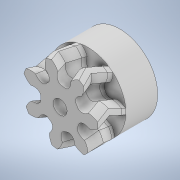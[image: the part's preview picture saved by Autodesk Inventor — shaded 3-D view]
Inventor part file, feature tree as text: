
AUTODESK INVENTOR PART (.ipt)
format: ipt  version: 2022 (Build 260153070, 153G)  size: 865,792 bytes
history: native  units: mm
features: sketch x5, extrude x3, helix x2, pattern_circular x1, mirror x1, revolve x1, projected_geometry x1
ambient origin geometry x8: Origin, YZ Plane, XZ Plane, XY Plane, X Axis, Y Axis, Z Axis, Center Point
bodies: Solid1 (feature_tree)
feature tree (14):
  sketch  "Sketch1"  dims[d0=1.5mm d1=0.0mm]
  extrude  "Extrusion1"  TaperAngle=0.0deg  [1 undecoded]
  helix  "Coil1"  [1 undecoded]
  pattern_circular  "Circular Pattern1"  [2 undecoded]
  mirror  "Mirror1"
  helix  "Coil2"  [1 undecoded]
  extrude  "Extrusion2"  Depth=2.15mm
  extrude  "Extrusion3"  Depth=2.15mm
  revolve  "Revolution1"  Angle=90.0deg
  sketch  "Sketch2"  dims[d2=64.295707mm d3=1.5mm d4=10.0mm d5=0.0mm d6=90.0deg d7=90.0deg d8=0.0mm d9=0.0mm d10=70.0mm d11=360.0deg]
  projected_geometry  "Projected Loop1"
  sketch  "Sketch3"  dims[d13=64.295707mm d14=0.5mm d15=10.0mm d16=0.0mm d17=90.0deg d18=90.0deg d19=0.0mm d20=0.0mm]
  sketch  "Sketch4"  dims[d21=4.0mm d22=0.0mm]
  sketch  "Sketch5"  dims[d23=6.2mm d24=2.0mm d25=0.0mm d26=0.875mm d27=1.5mm d28=2.15mm d29=90.0deg]
note: 5 required parameter values undecoded (feature->parameter linkage not recoverable at this tier; creation-order binding heuristic only, values carry confidence <= 0.55)
